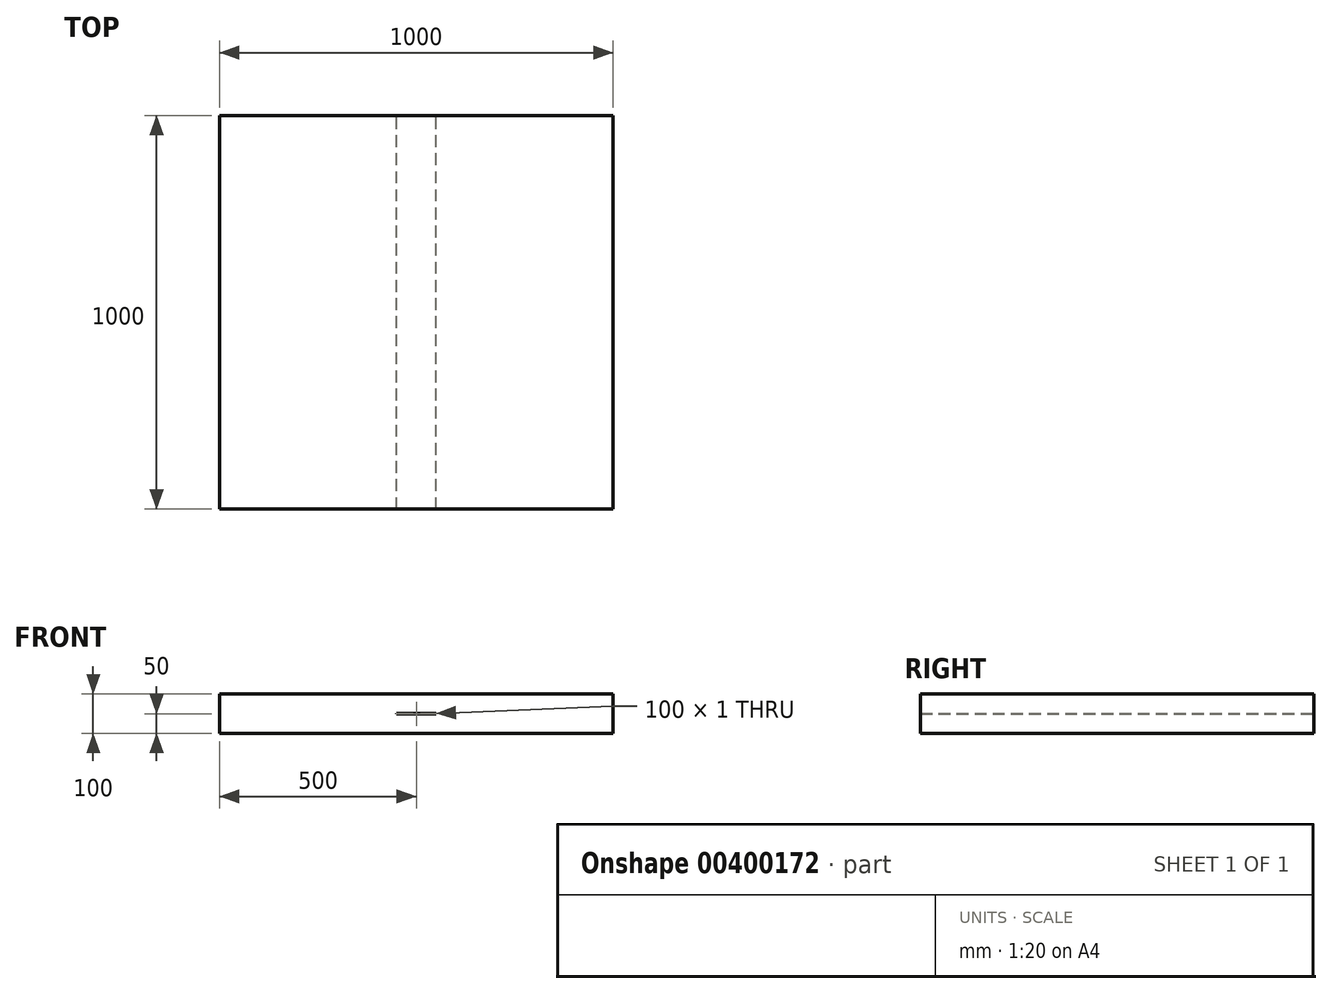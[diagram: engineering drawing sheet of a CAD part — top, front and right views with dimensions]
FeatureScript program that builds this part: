
annotation { "Feature Type Name" : "Feature", "Feature Type Description" : "" }
export const myFeature = defineFeature(function(context is Context, id is Id, definition is map)
    precondition{}
    {
        {
            var Q0;
            Q0=qCreatedBy(makeId("Front.planeOp"),FACE);
            var sketch = newSketch(context, id + "F0", { "sketchPlane" : qUnion([Q0])});
            skLineSegment(sketch, "E0.bottom", {"start": v(500, -50) * mm, "end": v(-500, -50) * mm});
            skLineSegment(sketch, "E0.top", {"start": v(500, 50) * mm, "end": v(-500, 50) * mm});
            skLineSegment(sketch, "E0.left", {"start": v(500, -50) * mm, "end": v(500, 50) * mm});
            skLineSegment(sketch, "E0.right", {"start": v(-500, -50) * mm, "end": v(-500, 50) * mm});
            skPoint(sketch, "E0.middle", {"position": v(0, 0) * mm});
            skLineSegment(sketch, "E1.bottom", {"start": v(50, -0.5) * mm, "end": v(-50, -0.5) * mm});
            skLineSegment(sketch, "E1.top", {"start": v(50, 0.5) * mm, "end": v(-50, 0.5) * mm});
            skLineSegment(sketch, "E1.left", {"start": v(50, -0.5) * mm, "end": v(50, 0.5) * mm});
            skLineSegment(sketch, "E1.right", {"start": v(-50, -0.5) * mm, "end": v(-50, 0.5) * mm});
            skSolve(sketch);
        }
        {
            var Q0;
            Q0 = qSketchRegion(id + "F0", true);
            extrude(context, id + "F1", {"entities" : qUnion([Q0]), "depth" : 500 * mm, "hasSecondDirection" : true, "secondDirectionOppositeDirection" : true, "secondDirectionDepth" : 500 * mm});
        }
    });
